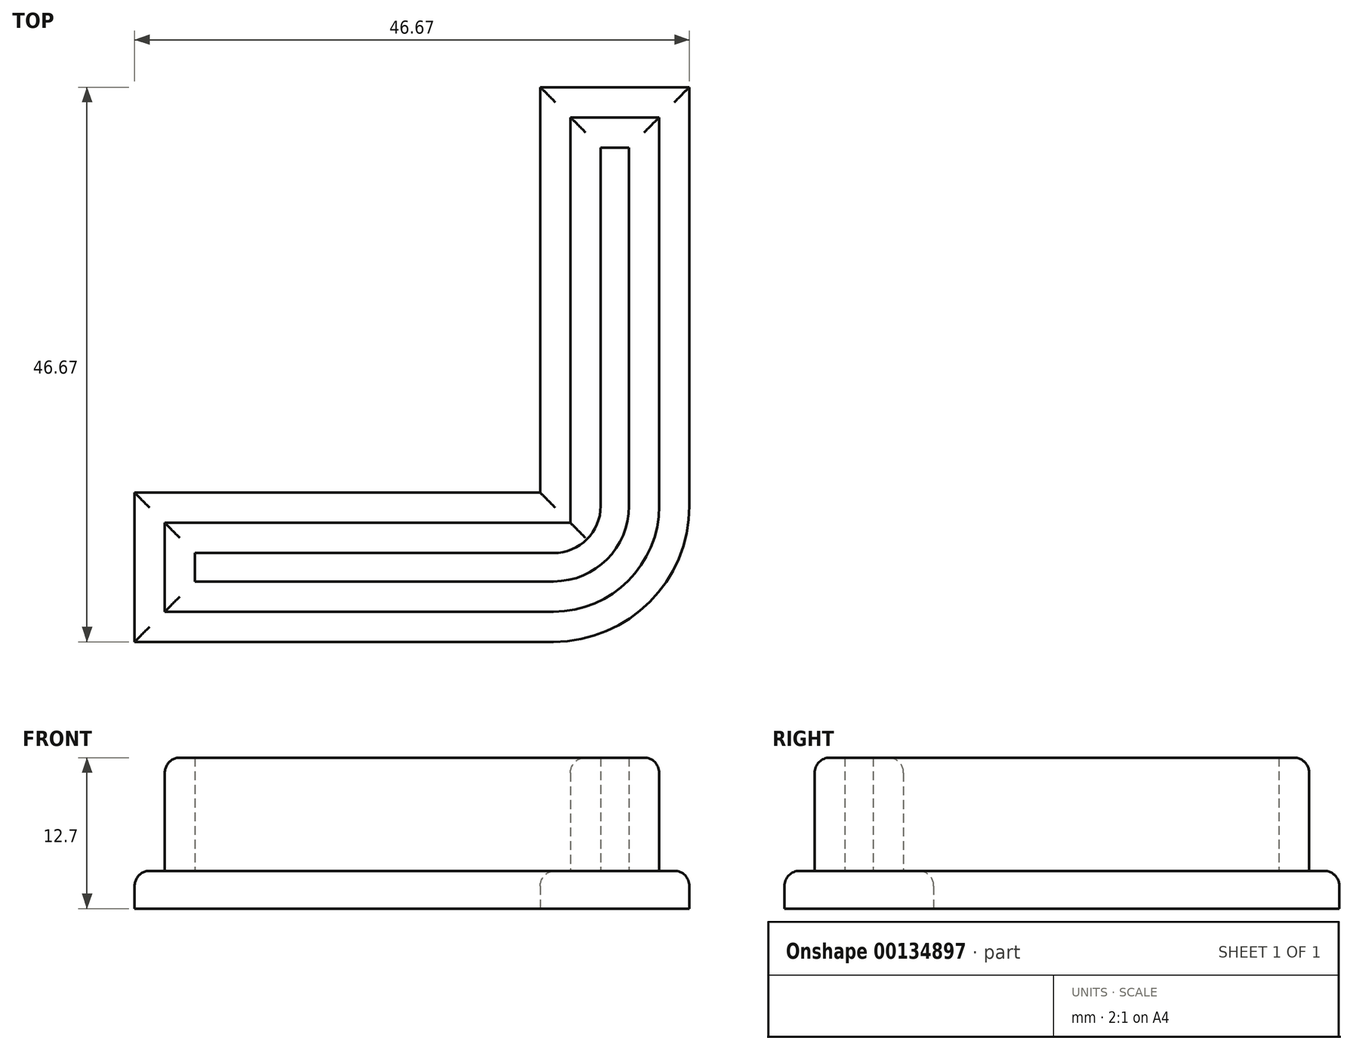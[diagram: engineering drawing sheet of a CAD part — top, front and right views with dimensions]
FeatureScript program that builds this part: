
annotation { "Feature Type Name" : "Feature", "Feature Type Description" : "" }
export const myFeature = defineFeature(function(context is Context, id is Id, definition is map)
    precondition{}
    {
        {
            var Q0;
            Q0=qCreatedBy(makeId("Top.planeOp"),FACE);
            var sketch = newSketch(context, id + "F0", { "sketchPlane" : qUnion([Q0])});
            skLineSegment(sketch, "E0.bottom", {"start": v(-6.35, 0) * mm, "end": v(-36.51, 0) * mm});
            skLineSegment(sketch, "E0.top", {"start": v(0, 36.51) * mm, "end": v(-36.51, 36.51) * mm});
            skLineSegment(sketch, "E0.left", {"start": v(0, 6.35) * mm, "end": v(0, 36.51) * mm});
            skLineSegment(sketch, "E0.right", {"start": v(-36.51, 0) * mm, "end": v(-36.51, 36.51) * mm});
            skPoint(sketch, "E1.visualSharp", {"position": v(0, 0) * mm});
            skArc(sketch, "E1.filletArc", {"start": v(-6.35, 0) * mm, "mid": v(-1.86, 1.86) * mm, "end": v(0, 6.35) * mm});
            skLineSegment(sketch, "E2.0", {"start": v(-34.12, 2.39) * mm, "end": v(-34.12, 34.12) * mm});
            skLineSegment(sketch, "E2.1", {"start": v(-2.39, 34.12) * mm, "end": v(-34.12, 34.12) * mm});
            skLineSegment(sketch, "E2.2", {"start": v(-6.35, 2.39) * mm, "end": v(-34.12, 2.39) * mm});
            skArc(sketch, "E2.3", {"start": v(-6.35, 2.39) * mm, "mid": v(-3.55, 3.55) * mm, "end": v(-2.39, 6.35) * mm});
            skLineSegment(sketch, "E2.4", {"start": v(-2.39, 6.35) * mm, "end": v(-2.39, 34.12) * mm});
            skLineSegment(sketch, "E3", {"start": v(-2.39, 34.12) * mm, "end": v(-2.39, 36.51) * mm});
            skLineSegment(sketch, "E4", {"start": v(-2.39, 36.51) * mm, "end": v(0, 36.51) * mm});
            skLineSegment(sketch, "E5", {"start": v(-34.12, 2.39) * mm, "end": v(-36.51, 2.39) * mm});
            skLineSegment(sketch, "E6", {"start": v(-36.51, 2.39) * mm, "end": v(-36.51, 0) * mm});
            skLineSegment(sketch, "E7.0", {"start": v(-34.12, 7.47) * mm, "end": v(-41.6, 7.47) * mm});
            skLineSegment(sketch, "E7.1", {"start": v(-7.47, 7.47) * mm, "end": v(-34.12, 7.47) * mm});
            skLineSegment(sketch, "E7.2", {"start": v(-41.6, 7.47) * mm, "end": v(-41.6, -5.08) * mm});
            skLineSegment(sketch, "E7.3", {"start": v(-7.47, 7.47) * mm, "end": v(-7.47, 34.12) * mm});
            skLineSegment(sketch, "E7.4", {"start": v(-7.47, 34.12) * mm, "end": v(-7.47, 41.6) * mm});
            skLineSegment(sketch, "E7.5", {"start": v(-6.35, -5.08) * mm, "end": v(-41.6, -5.08) * mm});
            skArc(sketch, "E7.6", {"start": v(-6.35, -5.08) * mm, "mid": v(1.73, -1.73) * mm, "end": v(5.08, 6.35) * mm});
            skLineSegment(sketch, "E7.7", {"start": v(5.08, 6.35) * mm, "end": v(5.08, 41.6) * mm});
            skLineSegment(sketch, "E7.8", {"start": v(-7.47, 41.6) * mm, "end": v(5.08, 41.6) * mm});
            skLineSegment(sketch, "E8.0", {"start": v(-34.12, 4.93) * mm, "end": v(-39.05, 4.93) * mm});
            skLineSegment(sketch, "E8.1", {"start": v(-4.93, 4.93) * mm, "end": v(-34.12, 4.93) * mm});
            skLineSegment(sketch, "E8.2", {"start": v(-39.05, 4.93) * mm, "end": v(-39.05, -2.54) * mm});
            skLineSegment(sketch, "E8.3", {"start": v(-4.93, 4.93) * mm, "end": v(-4.93, 34.12) * mm});
            skLineSegment(sketch, "E8.4", {"start": v(-4.93, 34.12) * mm, "end": v(-4.93, 39.05) * mm});
            skLineSegment(sketch, "E8.5", {"start": v(-6.35, -2.54) * mm, "end": v(-39.05, -2.54) * mm});
            skArc(sketch, "E8.6", {"start": v(-6.35, -2.54) * mm, "mid": v(-0.06, 0.06) * mm, "end": v(2.54, 6.35) * mm});
            skLineSegment(sketch, "E8.7", {"start": v(2.54, 6.35) * mm, "end": v(2.54, 39.05) * mm});
            skLineSegment(sketch, "E8.8", {"start": v(-4.93, 39.05) * mm, "end": v(2.54, 39.05) * mm});
            skSolve(sketch);
        }
        {
            var Q0;
            {var subQ3=sQuery(id+"F0.wireOp",EDGE,"E7.1");Q0=makeQuery(id+"F0.imprint","IMPRINT",FACE,{"disambiguationData":[TD([[makeQuery(id+"F0.imprint","IMPRINT",EDGE,{"derivedFrom":subQ3}),1.0]])]});}
            var Q1;
            {var subQ0=sQuery(id+"F0.wireOp",EDGE,"E7.0");var subQ1=sQuery(id+"F0.wireOp",EDGE,"E0.right");var subQ2=makeQuery(id+"F0.imprint","INTERSECT",VERTEX,{"derivedFrom":[subQ1,subQ0]});Q1=makeQuery(id+"F0.imprint","IMPRINT",FACE,{"disambiguationData":[TD([[makeQuery(id+"F0.imprint","IMPRINT",EDGE,{"disambiguationData":[TD([[subQ2,1.0]])],"derivedFrom":subQ1}),-1.0]])]});}
            var Q2;
            {var subQ5=sQuery(id+"F0.wireOp",EDGE,"E7.2");Q2=makeQuery(id+"F0.imprint","IMPRINT",FACE,{"disambiguationData":[TD([[makeQuery(id+"F0.imprint","IMPRINT",EDGE,{"derivedFrom":subQ5}),1.0]])]});}
            var Q3;
            {var subQ3=sQuery(id+"F0.wireOp",EDGE,"E2.2");Q3=makeQuery(id+"F0.imprint","IMPRINT",FACE,{"disambiguationData":[TD([[makeQuery(id+"F0.imprint","IMPRINT",EDGE,{"derivedFrom":subQ3}),-1.0]])]});}
            var Q4;
            Q4=makeQuery(id+"F0.imprint","IMPRINT",FACE,{"disambiguationData":[TD([[makeQuery(id+"F0.imprint","IMPRINT",EDGE,{"derivedFrom":sQuery(id+"F0.wireOp",EDGE,"E0.bottom")}),-1.0]])]});
            var Q5;
            Q5=makeQuery(id+"F0.imprint","IMPRINT",FACE,{"disambiguationData":[TD([[makeQuery(id+"F0.imprint","IMPRINT",EDGE,{"derivedFrom":sQuery(id+"F0.wireOp",EDGE,"E0.bottom")}),1.0]])]});
            var Q6;
            {var subQ0=sQuery(id+"F0.wireOp",EDGE,"E5");Q6=makeQuery(id+"F0.imprint","IMPRINT",FACE,{"disambiguationData":[TD([[makeQuery(id+"F0.imprint","IMPRINT",EDGE,{"derivedFrom":subQ0}),-1.0]])]});}
            var Q7;
            {var subQ0=sQuery(id+"F0.wireOp",EDGE,"E3");Q7=makeQuery(id+"F0.imprint","IMPRINT",FACE,{"disambiguationData":[TD([[makeQuery(id+"F0.imprint","IMPRINT",EDGE,{"derivedFrom":subQ0}),1.0]])]});}
            var Q8;
            {var subQ0=sQuery(id+"F0.wireOp",EDGE,"E7.4");var subQ1=sQuery(id+"F0.wireOp",EDGE,"E0.top");var subQ2=makeQuery(id+"F0.imprint","INTERSECT",VERTEX,{"derivedFrom":[subQ1,subQ0]});Q8=makeQuery(id+"F0.imprint","IMPRINT",FACE,{"disambiguationData":[TD([[makeQuery(id+"F0.imprint","IMPRINT",EDGE,{"disambiguationData":[TD([[subQ2,1.0]])],"derivedFrom":subQ1}),1.0]])]});}
            extrude(context, id + "F1", {"entities" : qUnion([Q0, Q1, Q2, Q3, Q4, Q5, Q6, Q7, Q8]), "depth" : 3.17 * mm});
        }
        {
            var Q0;
            Q0=makeQuery(id+"F0.imprint","IMPRINT",FACE,{"disambiguationData":[TD([[makeQuery(id+"F0.imprint","IMPRINT",EDGE,{"derivedFrom":sQuery(id+"F0.wireOp",EDGE,"E0.bottom")}),1.0]])]});
            var Q1;
            {var subQ3=sQuery(id+"F0.wireOp",EDGE,"E2.2");Q1=makeQuery(id+"F0.imprint","IMPRINT",FACE,{"disambiguationData":[TD([[makeQuery(id+"F0.imprint","IMPRINT",EDGE,{"derivedFrom":subQ3}),-1.0]])]});}
            var Q2;
            {var subQ0=sQuery(id+"F0.wireOp",EDGE,"E5");Q2=makeQuery(id+"F0.imprint","IMPRINT",FACE,{"disambiguationData":[TD([[makeQuery(id+"F0.imprint","IMPRINT",EDGE,{"derivedFrom":subQ0}),-1.0]])]});}
            var Q3;
            {var subQ0=sQuery(id+"F0.wireOp",EDGE,"E3");Q3=makeQuery(id+"F0.imprint","IMPRINT",FACE,{"disambiguationData":[TD([[makeQuery(id+"F0.imprint","IMPRINT",EDGE,{"derivedFrom":subQ0}),1.0]])]});}
            extrude(context, id + "F2", {"entities" : qUnion([Q0, Q1, Q2, Q3]), "operationType" : NewBodyOperationType.ADD, "depth" : 12.7 * mm});
        }
        {
            var Q0;
            Q0=makeQuery(id+"F1.opExtrude","CAP_EDGE",EDGE,{"disambiguationData":[OSD([sQuery(id+"F0.wireOp",EDGE,"E7.7")])],"isStart":false});
            var Q1;
            Q1=makeQuery(id+"F1.opExtrude","CAP_EDGE",EDGE,{"disambiguationData":[OSD([sQuery(id+"F0.wireOp",EDGE,"E7.8")])],"isStart":false});
            var Q2;
            Q2=makeQuery(id+"F1.opExtrude","CAP_EDGE",EDGE,{"disambiguationData":[OSD([sQuery(id+"F0.wireOp",EDGE,"E7.3"),sQuery(id+"F0.wireOp",EDGE,"E7.4")])],"isStart":false});
            var Q3;
            Q3=makeQuery(id+"F1.opExtrude","CAP_EDGE",EDGE,{"disambiguationData":[OSD([sQuery(id+"F0.wireOp",EDGE,"E7.0"),sQuery(id+"F0.wireOp",EDGE,"E7.1")])],"isStart":false});
            var Q4;
            Q4=makeQuery(id+"F1.opExtrude","CAP_EDGE",EDGE,{"disambiguationData":[OSD([sQuery(id+"F0.wireOp",EDGE,"E7.2")])],"isStart":false});
            var Q5;
            Q5=makeQuery(id+"F2.opExtrude","CAP_EDGE",EDGE,{"disambiguationData":[OSD([sQuery(id+"F0.wireOp",EDGE,"E8.3"),sQuery(id+"F0.wireOp",EDGE,"E8.4")])],"isStart":false});
            var Q6;
            Q6=makeQuery(id+"F2.opExtrude","CAP_EDGE",EDGE,{"disambiguationData":[OSD([sQuery(id+"F0.wireOp",EDGE,"E8.8")])],"isStart":false});
            var Q7;
            Q7=makeQuery(id+"F2.opExtrude","CAP_EDGE",EDGE,{"disambiguationData":[OSD([sQuery(id+"F0.wireOp",EDGE,"E8.7")])],"isStart":false});
            var Q8;
            Q8=makeQuery(id+"F2.opExtrude","CAP_EDGE",EDGE,{"disambiguationData":[OSD([sQuery(id+"F0.wireOp",EDGE,"E8.0"),sQuery(id+"F0.wireOp",EDGE,"E8.1")])],"isStart":false});
            var Q9;
            Q9=makeQuery(id+"F2.opExtrude","CAP_EDGE",EDGE,{"disambiguationData":[OSD([sQuery(id+"F0.wireOp",EDGE,"E8.2")])],"isStart":false});
            fillet(context, id + "F3", {"entities" : qUnion([Q0, Q1, Q2, Q3, Q4, Q5, Q6, Q7, Q8, Q9]), "radius" : 1.27 * mm, "tangentPropagation" : true, "allowEdgeOverflow" : false});
        }
    });
